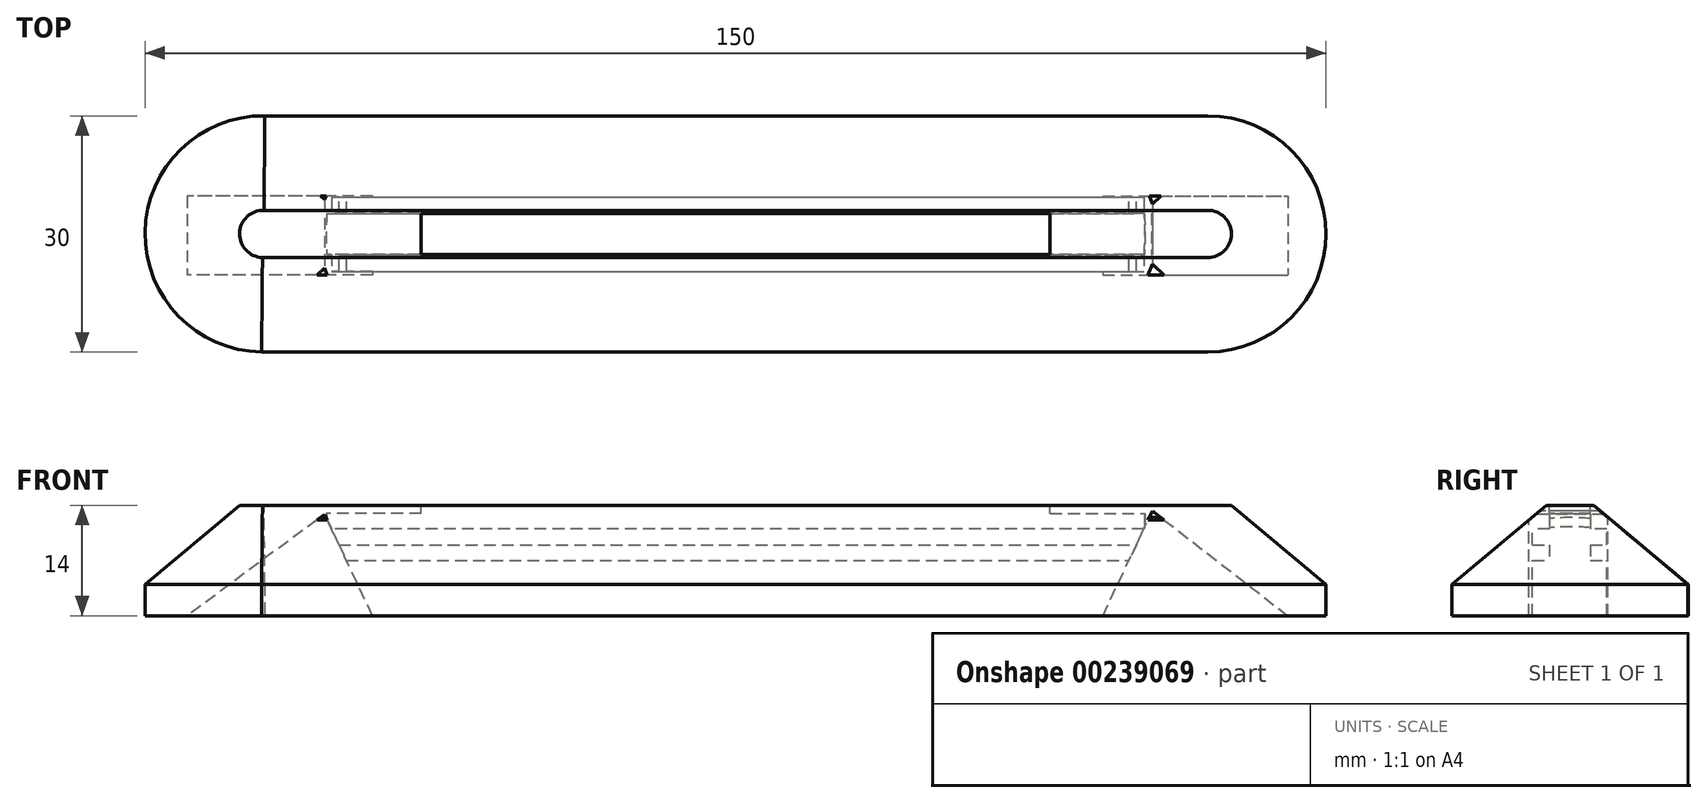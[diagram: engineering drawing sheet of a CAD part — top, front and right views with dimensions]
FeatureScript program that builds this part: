
annotation { "Feature Type Name" : "Feature", "Feature Type Description" : "" }
export const myFeature = defineFeature(function(context is Context, id is Id, definition is map)
    precondition{}
    {
        {
            var Q0;
            Q0=qCreatedBy(makeId("Top.planeOp"),FACE);
            var sketch = newSketch(context, id + "F0", { "sketchPlane" : qUnion([Q0])});
            skArc(sketch, "E0", {"start": v(-48.57, 17) * mm, "mid": v(-63.77, 2.2) * mm, "end": v(-48.96, -13) * mm});
            skArc(sketch, "E1", {"start": v(71.23, -13) * mm, "mid": v(86.23, 2) * mm, "end": v(71.23, 17) * mm});
            skLineSegment(sketch, "E2", {"start": v(-48.57, 17) * mm, "end": v(71.23, 17) * mm});
            skLineSegment(sketch, "E3", {"start": v(-48.96, -13) * mm, "end": v(71.23, -13) * mm});
            skLineSegment(sketch, "E4", {"start": v(-40.77, 2) * mm, "end": v(63.23, 2) * mm});
            skLineSegment(sketch, "E5", {"start": v(11.23, 2) * mm, "end": v(11.23, 4.6) * mm});
            skLineSegment(sketch, "E6", {"start": v(11.23, 2) * mm, "end": v(11.23, -0.6) * mm});
            skLineSegment(sketch, "E7", {"start": v(-40.7, 4.6) * mm, "end": v(63.17, 4.6) * mm});
            skLineSegment(sketch, "E8.MirrorCS", {"start": v(-40.7, -0.6) * mm, "end": v(63.17, -0.6) * mm});
            skArc(sketch, "E9", {"start": v(-40.7, 4.6) * mm, "mid": v(-40.77, 2) * mm, "end": v(-40.7, -0.6) * mm});
            skArc(sketch, "E10.trimOffspring", {"start": v(63.17, -0.6) * mm, "mid": v(63.23, 2) * mm, "end": v(63.17, 4.6) * mm});
            skPoint(sketch, "E11.orphan", {"position": v(-51.81, 4.6) * mm});
            skPoint(sketch, "E12.orphan", {"position": v(-51.81, -0.6) * mm});
            skPoint(sketch, "E13.orphan", {"position": v(74.93, 4.6) * mm});
            skPoint(sketch, "E14.orphan", {"position": v(74.93, -0.6) * mm});
            skSolve(sketch);
        }
        {
            var Q0;
            Q0 = qSketchRegion(id + "F0", true);
            extrude(context, id + "F1", {"entities" : qUnion([Q0]), "depth" : 14 * mm});
        }
        {
            var Q0;
            Q0=makeQuery(id+"F1.opExtrude","CAP_EDGE",EDGE,{"disambiguationData":[OSD([sQuery(id+"F0.wireOp",EDGE,"E0")])],"isStart":false});
            var Q1;
            Q1=makeQuery(id+"F1.opExtrude","CAP_EDGE",EDGE,{"disambiguationData":[OSD([sQuery(id+"F0.wireOp",EDGE,"E3")])],"isStart":false});
            var Q2;
            Q2=makeQuery(id+"F1.opExtrude","CAP_EDGE",EDGE,{"disambiguationData":[OSD([sQuery(id+"F0.wireOp",EDGE,"E2")])],"isStart":false});
            var Q3;
            Q3=makeQuery(id+"F1.opExtrude","CAP_EDGE",EDGE,{"disambiguationData":[OSD([sQuery(id+"F0.wireOp",EDGE,"E1")])],"isStart":false});
            chamfer(context, id + "F2", {"entities" : qUnion([Q0, Q1, Q2, Q3]), "chamferType" : ChamferType.TWO_OFFSETS, "width1" : 10 * mm, "oppositeDirection" : false, "width2" : 12 * mm, "tangentPropagation" : true});
        }
        {
            var Q0;
            Q0=makeQuery(id+"F1.opExtrude","CAP_FACE",FACE,{"disambiguationData":[OSD([sQuery(id+"F0.wireOp",EDGE,"E0"),sQuery(id+"F0.wireOp",EDGE,"E1"),sQuery(id+"F0.wireOp",EDGE,"E2"),sQuery(id+"F0.wireOp",EDGE,"E3"),sQuery(id+"F0.wireOp",EDGE,"E7"),sQuery(id+"F0.wireOp",EDGE,"E8.MirrorCS"),sQuery(id+"F0.wireOp",EDGE,"E9"),sQuery(id+"F0.wireOp",EDGE,"E10.trimOffspring")])],"isStart":true});
            var sketch = newSketch(context, id + "F3", { "sketchPlane" : qUnion([Q0])});
            skLineSegment(sketch, "E15.bottom", {"start": v(-42.77, -6.69) * mm, "end": v(65.23, -6.69) * mm});
            skLineSegment(sketch, "E15.top", {"start": v(-42.77, 2.77) * mm, "end": v(65.23, 2.77) * mm});
            skLineSegment(sketch, "E15.left", {"start": v(-42.77, -6.69) * mm, "end": v(-42.77, 2.77) * mm});
            skLineSegment(sketch, "E15.right", {"start": v(65.23, -6.69) * mm, "end": v(65.23, 2.77) * mm});
            skSolve(sketch);
        }
        {
            var Q0;
            Q0 = qSketchRegion(id + "F3", true);
            extrude(context, id + "F4", {"entities" : qUnion([Q0]), "operationType" : NewBodyOperationType.REMOVE, "depth" : 11 * mm, "hasSecondDirection" : true, "secondDirectionOppositeDirection" : true, "secondDirectionDepth" : 11 * mm});
        }
        {
            var Q0;
            Q0=makeQuery(id+"F0.imprint","IMPRINT",FACE,{"disambiguationData":[TD([[makeQuery(id+"F0.imprint","IMPRINT",EDGE,{"derivedFrom":sQuery(id+"F0.wireOp",EDGE,"E0")}),1.0]])]});
            var sketch = newSketch(context, id + "F5", { "sketchPlane" : qUnion([Q0])});
            skLineSegment(sketch, "E16.0", {"start": v(-42.77, 6.69) * mm, "end": v(-42.77, -2.77) * mm});
            skLineSegment(sketch, "E16.1", {"start": v(-42.77, 6.69) * mm, "end": v(65.23, 6.69) * mm});
            skLineSegment(sketch, "E16.2", {"start": v(-40.7, 4.6) * mm, "end": v(63.17, 4.6) * mm});
            skLineSegment(sketch, "E16.3", {"start": v(-40.7, -0.6) * mm, "end": v(63.17, -0.6) * mm});
            skArc(sketch, "E16.4", {"start": v(-40.7, 4.6) * mm, "mid": v(-40.77, 2) * mm, "end": v(-40.7, -0.6) * mm});
            skLineSegment(sketch, "E16.5", {"start": v(-42.77, -2.77) * mm, "end": v(65.23, -2.77) * mm});
            skArc(sketch, "E16.6", {"start": v(63.17, -0.6) * mm, "mid": v(63.23, 2) * mm, "end": v(63.17, 4.6) * mm});
            skLineSegment(sketch, "E16.7", {"start": v(65.23, 6.69) * mm, "end": v(65.23, -2.77) * mm});
            skSolve(sketch);
        }
        {
            var Q0;
            Q0 = qSketchRegion(id + "F5", true);
            extrude(context, id + "F6", {"entities" : qUnion([Q0]), "operationType" : NewBodyOperationType.ADD, "depth" : 9 * mm, "hasSecondDirection" : true, "secondDirectionOppositeDirection" : false, "secondDirectionDepth" : 7 * mm});
        }
        {
            var Q0;
            Q0=qCreatedBy(makeId("Front.planeOp"),FACE);
            var sketch = newSketch(context, id + "F7", { "sketchPlane" : qUnion([Q0])});
            skLineSegment(sketch, "E17.bottom", {"start": v(-34.89, 0) * mm, "end": v(-58.4, 0) * mm});
            skLineSegment(sketch, "E17.left", {"start": v(-34.89, 0) * mm, "end": v(-40.96, 12.88) * mm});
            skLineSegment(sketch, "E18", {"start": v(-40.96, 12.88) * mm, "end": v(-58.4, 0) * mm});
            skLineSegment(sketch, "E19.MirrorCS", {"start": v(57.88, 0) * mm, "end": v(81.38, 0) * mm});
            skLineSegment(sketch, "E20.MirrorCS", {"start": v(64.19, 13.32) * mm, "end": v(81.38, 0) * mm});
            skLineSegment(sketch, "E21.MirrorCS", {"start": v(57.88, 0) * mm, "end": v(64.19, 13.32) * mm});
            skSolve(sketch);
        }
        {
            var Q0;
            Q0 = qSketchRegion(id + "F7", true);
            extrude(context, id + "F8", {"entities" : qUnion([Q0]), "operationType" : NewBodyOperationType.REMOVE, "oppositeDirection" : true, "depth" : 6.8 * mm, "hasSecondDirection" : true, "secondDirectionOppositeDirection" : false, "secondDirectionDepth" : 3.2 * mm});
        }
        {
            var Q0;
            Q0=makeQuery(id+"F1.opExtrude","CAP_FACE",FACE,{"disambiguationData":[OSD([sQuery(id+"F0.wireOp",EDGE,"E0"),sQuery(id+"F0.wireOp",EDGE,"E1"),sQuery(id+"F0.wireOp",EDGE,"E2"),sQuery(id+"F0.wireOp",EDGE,"E3"),sQuery(id+"F0.wireOp",EDGE,"E7"),sQuery(id+"F0.wireOp",EDGE,"E8.MirrorCS"),sQuery(id+"F0.wireOp",EDGE,"E9"),sQuery(id+"F0.wireOp",EDGE,"E10.trimOffspring")])],"isStart":false});
            var sketch = newSketch(context, id + "F9", { "sketchPlane" : qUnion([Q0])});
            skLineSegment(sketch, "E22.bottom", {"start": v(-41.7, 4.6) * mm, "end": v(-28.7, 4.6) * mm});
            skLineSegment(sketch, "E22.top", {"start": v(-41.7, -0.6) * mm, "end": v(-28.7, -0.6) * mm});
            skLineSegment(sketch, "E22.left", {"start": v(-41.7, 4.6) * mm, "end": v(-41.7, -0.6) * mm});
            skLineSegment(sketch, "E22.right", {"start": v(-28.7, 4.6) * mm, "end": v(-28.7, -0.6) * mm});
            skLineSegment(sketch, "E23.bottom", {"start": v(63.17, -0.6) * mm, "end": v(51.17, -0.6) * mm});
            skLineSegment(sketch, "E23.top", {"start": v(64.17, 4.6) * mm, "end": v(51.17, 4.6) * mm});
            skLineSegment(sketch, "E23.left", {"start": v(64.17, -0.6) * mm, "end": v(64.17, 4.6) * mm});
            skLineSegment(sketch, "E23.right", {"start": v(51.17, -0.6) * mm, "end": v(51.17, 4.6) * mm});
            skLineSegment(sketch, "E24", {"start": v(64.17, -0.6) * mm, "end": v(63.17, -0.6) * mm});
            skSolve(sketch);
        }
        {
            var Q0;
            Q0 = qSketchRegion(id + "F9", true);
            extrude(context, id + "F10", {"entities" : qUnion([Q0]), "operationType" : NewBodyOperationType.ADD, "oppositeDirection" : true, "depth" : 1 * mm});
        }
    });
